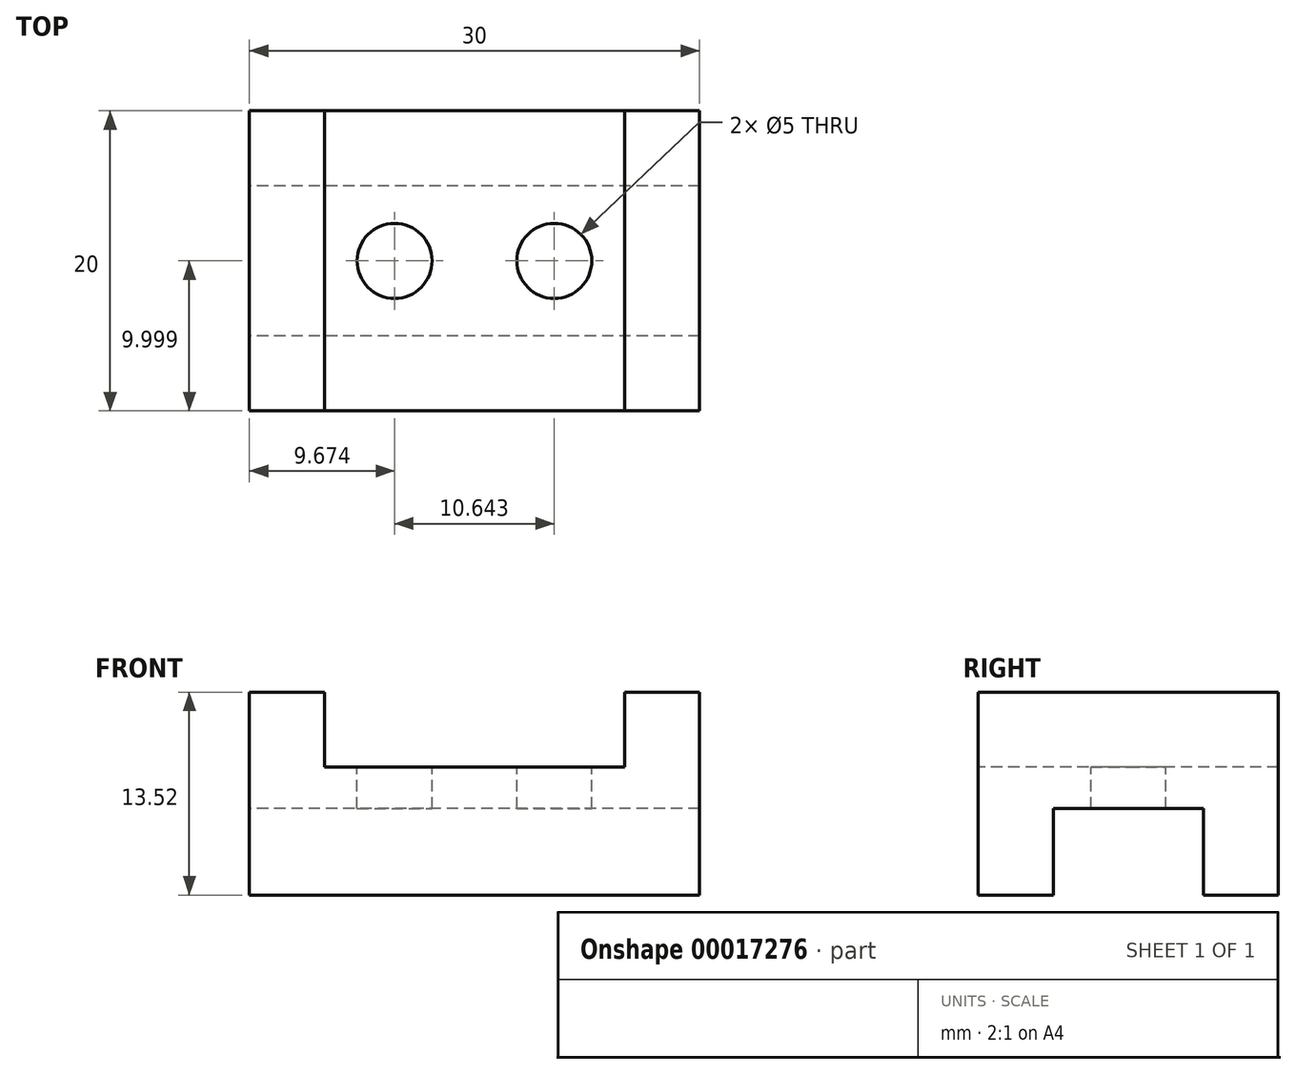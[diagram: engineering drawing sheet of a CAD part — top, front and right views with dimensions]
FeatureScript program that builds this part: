
annotation { "Feature Type Name" : "Feature", "Feature Type Description" : "" }
export const myFeature = defineFeature(function(context is Context, id is Id, definition is map)
    precondition{}
    {
        {
            var Q0;
            Q0=qCreatedBy(makeId("Right.planeOp"),FACE);
            var sketch = newSketch(context, id + "F0", { "sketchPlane" : qUnion([Q0])});
            skLineSegment(sketch, "E0", {"start": v(-11.68, -5.77) * mm, "end": v(-11.68, 7.75) * mm});
            skLineSegment(sketch, "E1", {"start": v(-11.68, 7.75) * mm, "end": v(8.32, 7.75) * mm});
            skLineSegment(sketch, "E2", {"start": v(8.32, 7.75) * mm, "end": v(8.32, -5.77) * mm});
            skLineSegment(sketch, "E3", {"start": v(8.32, -5.77) * mm, "end": v(3.32, -5.77) * mm});
            skLineSegment(sketch, "E4", {"start": v(3.32, -5.77) * mm, "end": v(3.32, 0) * mm});
            skLineSegment(sketch, "E5", {"start": v(3.32, 0) * mm, "end": v(-6.68, 0) * mm});
            skLineSegment(sketch, "E6", {"start": v(-6.68, 0) * mm, "end": v(-6.68, -5.77) * mm});
            skLineSegment(sketch, "E7", {"start": v(-6.68, -5.77) * mm, "end": v(-11.68, -5.77) * mm});
            skSolve(sketch);
        }
        {
            var Q0;
            Q0=makeQuery(id+"F0.imprint","IMPRINT",FACE,{"disambiguationData":[TD([[makeQuery(id+"F0.imprint","IMPRINT",EDGE,{"derivedFrom":sQuery(id+"F0.wireOp",EDGE,"E0")}),-1.0]])]});
            extrude(context, id + "F1", {"entities" : qUnion([Q0]), "depth" : 30 * mm});
        }
        {
            var Q0;
            Q0=makeQuery(id+"F1.opExtrude","SWEPT_FACE",FACE,{"disambiguationData":[OSD([sQuery(id+"F0.wireOp",EDGE,"E0")])]});
            var sketch = newSketch(context, id + "F2", { "sketchPlane" : qUnion([Q0])});
            skLineSegment(sketch, "E8", {"start": v(5, 7.75) * mm, "end": v(5, 2.75) * mm});
            skLineSegment(sketch, "E9", {"start": v(5, 2.75) * mm, "end": v(25, 2.75) * mm});
            skLineSegment(sketch, "E10", {"start": v(25, 2.75) * mm, "end": v(25, 7.75) * mm});
            skLineSegment(sketch, "E11", {"start": v(25, 7.75) * mm, "end": v(5, 7.75) * mm});
            skLineSegment(sketch, "E12", {"start": v(0, 7.75) * mm, "end": v(5, 7.75) * mm});
            skLineSegment(sketch, "E13", {"start": v(25, 7.75) * mm, "end": v(30, 7.75) * mm});
            skSolve(sketch);
        }
        {
            var Q0;
            Q0=makeQuery(id+"F2.imprint","IMPRINT",FACE,{"disambiguationData":[TD([[makeQuery(id+"F2.imprint","IMPRINT",EDGE,{"derivedFrom":sQuery(id+"F2.wireOp",EDGE,"E8")}),1.0]])]});
            extrude(context, id + "F3", {"entities" : qUnion([Q0]), "operationType" : NewBodyOperationType.REMOVE, "oppositeDirection" : true, "depth" : 25 * mm});
        }
        {
            var Q0;
            Q0=makeQuery(id+"F3.boolean.opBoolean","COPY",FACE,{"derivedFrom":makeQuery(id+"F3.opExtrude","SWEPT_FACE",FACE,{"disambiguationData":[OSD([sQuery(id+"F2.wireOp",EDGE,"E9")])]})});
            var sketch = newSketch(context, id + "F4", { "sketchPlane" : qUnion([Q0])});
            skCircle(sketch, "E14", {"center": v(9.67, -1.68) * mm, "radius": 2.5 * mm});
            skCircle(sketch, "E15", {"center": v(20.32, -1.68) * mm, "radius": 2.5 * mm});
            skSolve(sketch);
        }
        {
            var Q0;
            Q0 = qSketchRegion(id + "F4", true);
            extrude(context, id + "F5", {"entities" : qUnion([Q0]), "operationType" : NewBodyOperationType.REMOVE, "oppositeDirection" : true, "depth" : 25 * mm});
        }
    });
